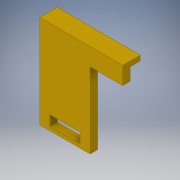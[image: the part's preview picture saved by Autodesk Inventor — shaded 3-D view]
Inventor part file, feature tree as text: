
AUTODESK INVENTOR PART (.ipt)
format: ipt  version: 2019 (Build 230136000, 136)  size: 312,320 bytes
history: native  units: mm
features: extrude x6, sketch x6, projected_geometry x4, other x3, reference x2, chamfer x1
ambient origin geometry x8: Origin, YZ Plane, XZ Plane, XY Plane, X Axis, Y Axis, Z Axis, Center Point
bodies: Solid1 (feature_tree)
feature tree (22):
  extrude  "Extrusion1"  Depth=3.0mm TaperAngle=0.0deg
  extrude  "Extrusion2"  Depth=4.0mm
  extrude  "Extrusion3"  Depth=12.0mm
  extrude  "Extrusion5"  Depth=4.0mm
  chamfer  "Chamfer1"  Distance=4.0mm
  extrude  "Extrusion6"  Depth=2.0mm
  extrude  "Extrusion4"  Depth=4.0mm
  sketch  "Sketch1"  dims[d1=45.0mm d2=3.0mm d3=0.0mm]
  reference  "Reference1"
  sketch  "Sketch2"  dims[d4=4.0mm d5=0.0mm d7=45.842722mm]
  reference  "Reference2"
  projected_geometry  "Projected Loop1"
  sketch  "Sketch3"  dims[d8=22.93mm d9=12.0mm]
  sketch  "Sketch4"  dims[d10=4.0mm d11=4.0mm]
  projected_geometry  "Projected Loop2"
  sketch  "Sketch5"  dims[d12=3.5mm]
  projected_geometry  "Projected Loop3"
  sketch  "Sketch6"  dims[d13=3.5mm d21=4.0mm d22=0.0mm d23=22.93mm d24=4.0mm d25=4.0mm d26=3.0mm d27=5.0mm d28=40.0mm d30=9.0mm d31=10.0mm d33=10.0mm d35=13.0mm d36=0.0mm d37=4.0mm d38=0.0mm d39=30.0mm d40=4.0mm d41=8.75mm d42=2.0mm d43=45.0deg d44=8.0mm d45=12.5mm d46=0.0mm]
  projected_geometry  "Projected Loop4"
  parser-record x1  (decoder bookkeeping rows leaked as tree rows — omitted from the tree; the rows remain in map.json)
  other  "Aligner Helper Assembly.iam"
  other  "Base v6 - 175:2"
note: 1 file-system path scrubbed to <path> (originals preserved in map.json)
